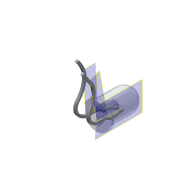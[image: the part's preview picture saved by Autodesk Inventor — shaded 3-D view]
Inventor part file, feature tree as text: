
AUTODESK INVENTOR PART (.ipt)
format: ipt  version: 2016 (Build 200138000, 138)  size: 370,688 bytes
history: native  units: mm
features: other x6, sketch x5, plane x3
ambient origin geometry x8: Origin, YZ Plane, XZ Plane, XY Plane, X Axis, Y Axis, Z Axis, Center Point
bodies: Solid1 (feature_tree), Solid2 (feature_tree)
feature tree (14):
  other  "5mm LED.ipt"
  other  "Solid1::5mm LED.ipt"
  other  "Solid2::5mm LED.ipt"
  other  "TaggingFeature1"
  sketch  "Sketch1"  dims[d0=10.0mm]
  sketch  "Sketch2"
  sketch  "Sketch4"
  sketch  "Sketch5"
  sketch  "Sketch6"
  plane  "Work Plane1"
  plane  "Work Plane2"
  plane  "Work Plane3"
  other  "Work Point1"
  other  "Work Point2"
